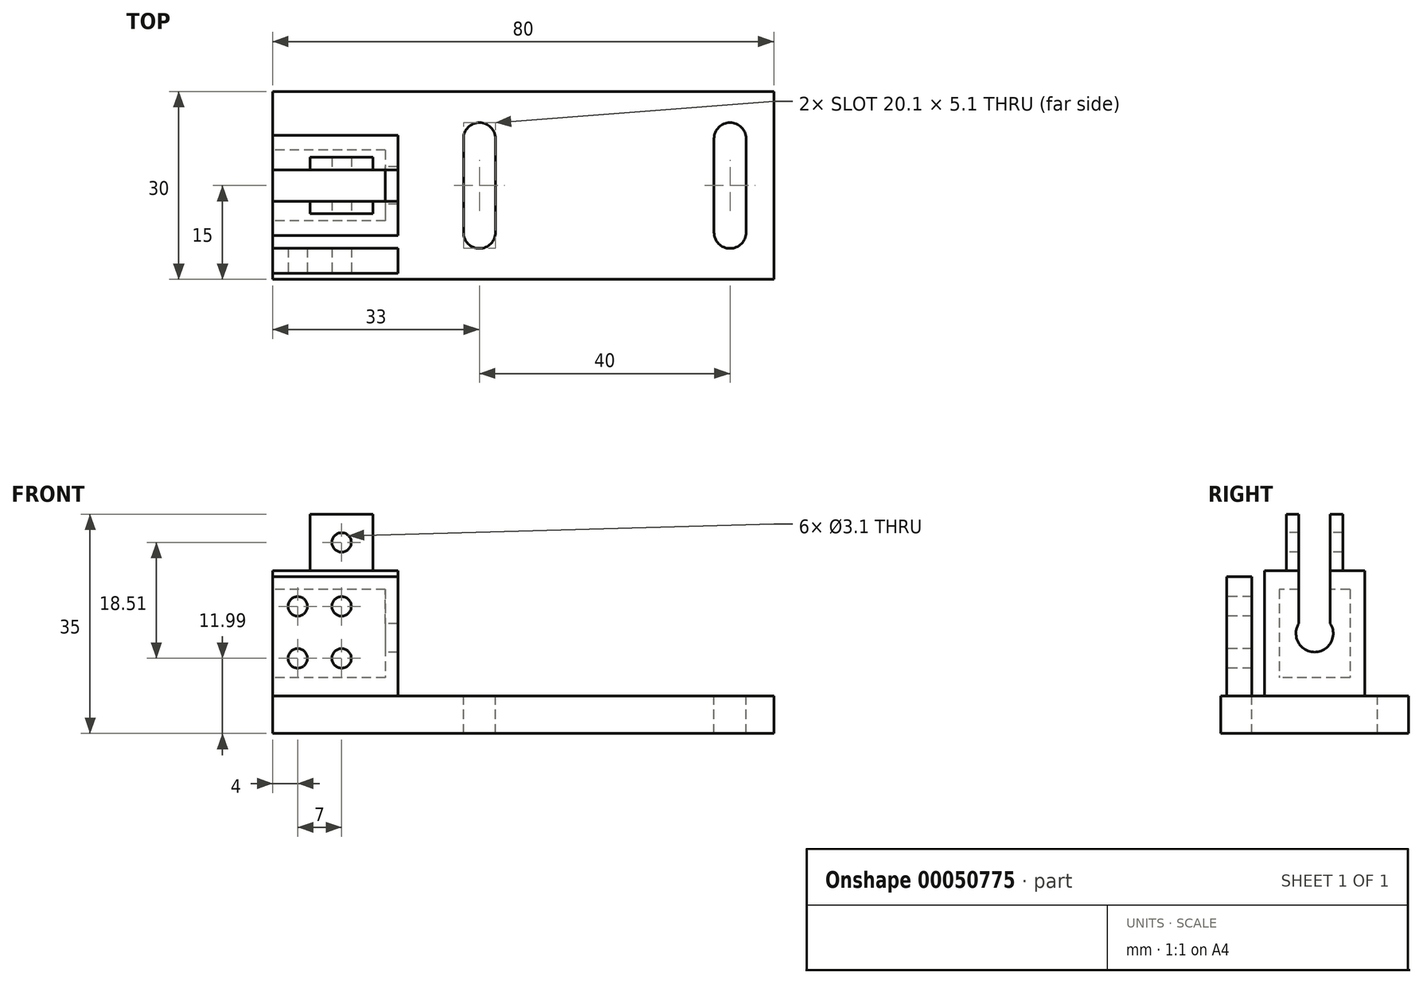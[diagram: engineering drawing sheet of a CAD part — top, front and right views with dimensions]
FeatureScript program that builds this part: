
annotation { "Feature Type Name" : "Feature", "Feature Type Description" : "" }
export const myFeature = defineFeature(function(context is Context, id is Id, definition is map)
    precondition{}
    {
        {
            var Q0;
            Q0=qCreatedBy(makeId("Top.planeOp"),FACE);
            var sketch = newSketch(context, id + "F0", { "sketchPlane" : qUnion([Q0])});
            skLineSegment(sketch, "E0.bottom", {"start": v(-40, 15) * mm, "end": v(40, 15) * mm});
            skLineSegment(sketch, "E0.top", {"start": v(-40, -15) * mm, "end": v(40, -15) * mm});
            skLineSegment(sketch, "E0.left", {"start": v(-40, 15) * mm, "end": v(-40, -15) * mm});
            skLineSegment(sketch, "E0.right", {"start": v(40, 15) * mm, "end": v(40, -15) * mm});
            skSolve(sketch);
        }
        {
            var Q0;
            Q0 = qSketchRegion(id + "F0", true);
            extrude(context, id + "F1", {"entities" : qUnion([Q0]), "depth" : 6 * mm});
        }
        {
            var Q0;
            Q0=makeQuery(id+"F1.opExtrude","CAP_FACE",FACE,{"disambiguationData":[OSD([sQuery(id+"F0.wireOp",EDGE,"E0.bottom"),sQuery(id+"F0.wireOp",EDGE,"E0.top"),sQuery(id+"F0.wireOp",EDGE,"E0.left"),sQuery(id+"F0.wireOp",EDGE,"E0.right")])],"isStart":false});
            var sketch = newSketch(context, id + "F2", { "sketchPlane" : qUnion([Q0])});
            skArc(sketch, "E1", {"start": v(35.55, 7.5) * mm, "mid": v(33, 10.05) * mm, "end": v(30.45, 7.5) * mm});
            skArc(sketch, "E2", {"start": v(-4.45, 7.5) * mm, "mid": v(-7, 10.05) * mm, "end": v(-9.55, 7.5) * mm});
            skArc(sketch, "E3", {"start": v(30.45, -7.5) * mm, "mid": v(33, -10.05) * mm, "end": v(35.55, -7.5) * mm});
            skArc(sketch, "E4", {"start": v(-9.55, -7.5) * mm, "mid": v(-7, -10.05) * mm, "end": v(-4.45, -7.5) * mm});
            skLineSegment(sketch, "E5.left", {"start": v(30.45, 7.5) * mm, "end": v(30.45, -7.5) * mm});
            skLineSegment(sketch, "E5.right", {"start": v(35.55, 7.5) * mm, "end": v(35.55, -7.5) * mm});
            skLineSegment(sketch, "E6.left", {"start": v(-9.55, 7.5) * mm, "end": v(-9.55, -7.5) * mm});
            skLineSegment(sketch, "E6.right", {"start": v(-4.45, 7.5) * mm, "end": v(-4.45, -7.5) * mm});
            skSolve(sketch);
        }
        {
            var Q0;
            Q0 = qSketchRegion(id + "F2", true);
            extrude(context, id + "F3", {"entities" : qUnion([Q0]), "operationType" : NewBodyOperationType.REMOVE, "endBound" : BoundingType.THROUGH_ALL, "oppositeDirection" : true, "depth" : 25 * mm});
        }
        {
            var Q0;
            Q0=makeQuery(id+"F1.opExtrude","CAP_FACE",FACE,{"disambiguationData":[OSD([sQuery(id+"F0.wireOp",EDGE,"E0.bottom"),sQuery(id+"F0.wireOp",EDGE,"E0.top"),sQuery(id+"F0.wireOp",EDGE,"E0.left"),sQuery(id+"F0.wireOp",EDGE,"E0.right")])],"isStart":false});
            var sketch = newSketch(context, id + "F4", { "sketchPlane" : qUnion([Q0])});
            skLineSegment(sketch, "E7.bottom", {"start": v(-40, 8) * mm, "end": v(-20, 8) * mm});
            skLineSegment(sketch, "E7.top", {"start": v(-40, -8) * mm, "end": v(-20, -8) * mm});
            skLineSegment(sketch, "E7.left", {"start": v(-40, 8) * mm, "end": v(-40, -8) * mm});
            skLineSegment(sketch, "E7.right", {"start": v(-20, 8) * mm, "end": v(-20, -8) * mm});
            skSolve(sketch);
        }
        {
            var Q0;
            Q0 = qSketchRegion(id + "F4", true);
            extrude(context, id + "F5", {"entities" : qUnion([Q0]), "operationType" : NewBodyOperationType.ADD, "depth" : 20 * mm});
        }
        {
            var Q0;
            Q0=makeQuery(id+"F5.boolean.opBoolean","MERGE",FACE,{"derivedFrom":[makeQuery(id+"F1.opExtrude","SWEPT_FACE",FACE,{"disambiguationData":[OSD([sQuery(id+"F0.wireOp",EDGE,"E0.left")])]}),makeQuery(id+"F5.opExtrude","SWEPT_FACE",FACE,{"disambiguationData":[OSD([sQuery(id+"F4.wireOp",EDGE,"E7.left")])]})]});
            var sketch = newSketch(context, id + "F6", { "sketchPlane" : qUnion([Q0])});
            skLineSegment(sketch, "E8.bottom", {"start": v(-5.63, 23) * mm, "end": v(5.64, 23) * mm});
            skLineSegment(sketch, "E8.top", {"start": v(-5.63, 8.92) * mm, "end": v(5.64, 8.92) * mm});
            skLineSegment(sketch, "E8.left", {"start": v(-5.63, 23) * mm, "end": v(-5.63, 8.92) * mm});
            skLineSegment(sketch, "E8.right", {"start": v(5.64, 23) * mm, "end": v(5.64, 8.92) * mm});
            skSolve(sketch);
        }
        {
            var Q0;
            Q0 = qSketchRegion(id + "F6", true);
            extrude(context, id + "F7", {"entities" : qUnion([Q0]), "operationType" : NewBodyOperationType.REMOVE, "oppositeDirection" : true, "depth" : 18 * mm});
        }
        {
            var Q0;
            Q0=makeQuery(id+"F7.boolean.opBoolean","COPY",FACE,{"derivedFrom":makeQuery(id+"F7.opExtrude","CAP_FACE",FACE,{"disambiguationData":[OSD([sQuery(id+"F6.wireOp",EDGE,"E8.bottom"),sQuery(id+"F6.wireOp",EDGE,"E8.top"),sQuery(id+"F6.wireOp",EDGE,"E8.left"),sQuery(id+"F6.wireOp",EDGE,"E8.right")])],"isStart":false})});
            var sketch = newSketch(context, id + "F8", { "sketchPlane" : qUnion([Q0])});
            skCircle(sketch, "E9", {"center": v(0, 15.96) * mm, "radius": 2.97 * mm});
            skSolve(sketch);
        }
        {
            var Q0;
            Q0 = qSketchRegion(id + "F8", true);
            extrude(context, id + "F9", {"entities" : qUnion([Q0]), "operationType" : NewBodyOperationType.REMOVE, "endBound" : BoundingType.THROUGH_ALL, "oppositeDirection" : true, "depth" : 25 * mm});
        }
        {
            var Q0;
            Q0=makeQuery(id+"F5.opExtrude","CAP_FACE",FACE,{"disambiguationData":[OSD([sQuery(id+"F4.wireOp",EDGE,"E7.bottom"),sQuery(id+"F4.wireOp",EDGE,"E7.top"),sQuery(id+"F4.wireOp",EDGE,"E7.left"),sQuery(id+"F4.wireOp",EDGE,"E7.right")])],"isStart":false});
            var sketch = newSketch(context, id + "F10", { "sketchPlane" : qUnion([Q0])});
            skLineSegment(sketch, "E10.bottom", {"start": v(-24, 4.5) * mm, "end": v(-34, 4.5) * mm});
            skLineSegment(sketch, "E10.top", {"start": v(-24, -4.5) * mm, "end": v(-34, -4.5) * mm});
            skLineSegment(sketch, "E10.left", {"start": v(-24, 4.5) * mm, "end": v(-24, -4.5) * mm});
            skLineSegment(sketch, "E10.right", {"start": v(-34, 4.5) * mm, "end": v(-34, -4.5) * mm});
            skSolve(sketch);
        }
        {
            var Q0;
            Q0 = qSketchRegion(id + "F10", true);
            extrude(context, id + "F11", {"entities" : qUnion([Q0]), "operationType" : NewBodyOperationType.ADD, "depth" : 9 * mm});
        }
        {
            var Q0;
            Q0=makeQuery(id+"F11.opExtrude","SWEPT_FACE",FACE,{"disambiguationData":[OSD([sQuery(id+"F10.wireOp",EDGE,"E10.top")])]});
            var sketch = newSketch(context, id + "F12", { "sketchPlane" : qUnion([Q0])});
            skCircle(sketch, "E11", {"center": v(-29, 30.5) * mm, "radius": 1.55 * mm});
            skSolve(sketch);
        }
        {
            var Q0;
            Q0 = qSketchRegion(id + "F12", true);
            extrude(context, id + "F13", {"entities" : qUnion([Q0]), "operationType" : NewBodyOperationType.REMOVE, "endBound" : BoundingType.THROUGH_ALL, "oppositeDirection" : true, "depth" : 25 * mm});
        }
        {
            var Q0;
            Q0=makeQuery(id+"F11.opExtrude","CAP_FACE",FACE,{"disambiguationData":[OSD([sQuery(id+"F10.wireOp",EDGE,"E10.bottom"),sQuery(id+"F10.wireOp",EDGE,"E10.top"),sQuery(id+"F10.wireOp",EDGE,"E10.left"),sQuery(id+"F10.wireOp",EDGE,"E10.right")])],"isStart":false});
            var sketch = newSketch(context, id + "F14", { "sketchPlane" : qUnion([Q0])});
            skLineSegment(sketch, "E12.bottom", {"start": v(-40, 2.5) * mm, "end": v(-20, 2.5) * mm});
            skLineSegment(sketch, "E12.top", {"start": v(-40, -2.5) * mm, "end": v(-20, -2.5) * mm});
            skLineSegment(sketch, "E12.left", {"start": v(-40, 2.5) * mm, "end": v(-40, -2.5) * mm});
            skLineSegment(sketch, "E12.right", {"start": v(-20, 2.5) * mm, "end": v(-20, -2.5) * mm});
            skSolve(sketch);
        }
        {
            var Q0;
            Q0 = qSketchRegion(id + "F14", true);
            extrude(context, id + "F15", {"entities" : qUnion([Q0]), "operationType" : NewBodyOperationType.REMOVE, "oppositeDirection" : true, "depth" : 19 * mm});
        }
        {
            var Q0;
            Q0=qCreatedBy(makeId("Top.planeOp"),FACE);
            var sketch = newSketch(context, id + "F16", { "sketchPlane" : qUnion([Q0])});
            skLineSegment(sketch, "E13.bottom", {"start": v(-40, -10) * mm, "end": v(-20, -10) * mm});
            skLineSegment(sketch, "E13.top", {"start": v(-40, -14) * mm, "end": v(-20, -14) * mm});
            skLineSegment(sketch, "E13.left", {"start": v(-40, -10) * mm, "end": v(-40, -14) * mm});
            skLineSegment(sketch, "E13.right", {"start": v(-20, -10) * mm, "end": v(-20, -14) * mm});
            skSolve(sketch);
        }
        {
            var Q0;
            Q0 = qSketchRegion(id + "F16", true);
            extrude(context, id + "F17", {"entities" : qUnion([Q0]), "operationType" : NewBodyOperationType.ADD, "depth" : 25 * mm});
        }
        {
            var Q0;
            Q0=makeQuery(id+"F17.opExtrude","SWEPT_FACE",FACE,{"disambiguationData":[OSD([sQuery(id+"F16.wireOp",EDGE,"E13.top")])]});
            var sketch = newSketch(context, id + "F18", { "sketchPlane" : qUnion([Q0])});
            skCircle(sketch, "E14", {"center": v(-36, 20.3) * mm, "radius": 1.55 * mm});
            skCircle(sketch, "E15", {"center": v(-36, 12) * mm, "radius": 1.55 * mm});
            skCircle(sketch, "E16", {"center": v(-29, 20.3) * mm, "radius": 1.55 * mm});
            skCircle(sketch, "E17", {"center": v(-29, 12) * mm, "radius": 1.55 * mm});
            skSolve(sketch);
        }
        {
            var Q0;
            Q0 = qSketchRegion(id + "F18", true);
            extrude(context, id + "F19", {"entities" : qUnion([Q0]), "operationType" : NewBodyOperationType.REMOVE, "oppositeDirection" : true, "depth" : 4 * mm});
        }
    });
